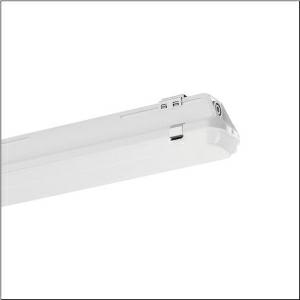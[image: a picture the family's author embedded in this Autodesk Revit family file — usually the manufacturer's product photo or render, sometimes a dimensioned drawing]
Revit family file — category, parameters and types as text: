
# Revit family: monsun_r__12_51fp209p460h_750e
name_source: partatom
category: Lighting Fixtures
units: mm (PartAtom-declared; Revit-internal decimal feet)

## family parameters
Cut with Voids When Loaded = No
Host = Face
Light Source = No
Part Type = Normal
Room Calculation Point = No
Round Connector Dimension = Use Diameter
Shared = No

## types (1)
- Monsun® 12 (1 x LED, 5490 lm, 34 W, 4000K)
    Apparent Load = 34 VA
    CIE Flux Codes = 45 75 93 94 100
    Color Rendering = 80
    Color Temperature = 4000K
    Default Elevation = 1800 mm
    Description = Monsun® 12, damp-proof luminaire, chain hanger, primary optical cover: enclosure, of PC, light emission: direct distribution, primary light characteristic: symmetric, installation type: suspended mounting, surface-mounted, horizontal mounting, vertical mounting, LED rated luminous flux: 5.490 lm, light colour: 840, colour temperature: 4000K, control gear: ECG, with terminal, 3-pole, max. 2.5mm², mains connection: 220..240V, AC, 50/60Hz, rated input power: 34W, luminaire housing, of glass-fibre reinforced polyester, uncoated, bright grey, length: 1.590 mm, width: 90 mm, height: 88mm, clip for enclosure, of stainless steel (V2A), ceiling mounting element, of stainless steel (V2A), chain hanger, of stainless steel (V2A), protection rating (complete): IP66, insulation class (complete): insulation class I (protective earthing), certification: CE, ENEC, VDE, protection symbol: D, impact resistance: IK08, permissible ambient temperature for indoor applications: -35..+40°C, standard: EN 50419, EN 60598-2-1, no direct snow, no direct sun, no direct rain, for indoor or canopied outdoor use, corresponds to IFS (International Featured Standards) requirements for safety and quality in the food industry, packaging unit: 1 piece
    Height = 89 mm
    Lamp = 1 x LED
    Lamp Light Flux = 5490 lm
    Lamp Power = 34 W
    Lamp count = 1
    Length = 1590 mm
    Luminous efficacy = 161 lm/W
    Manufacturer = Siteco
    ModVariant = No
    Model = 51FP209P460H
    Mounting Place = Ceiling
    Mounting Type = Pendant
    Number of Poles = 1
    OnlyDefault = Yes
    Power Factor = 1
    Product Name = Monsun® 12
    Product group = damp-proof luminaire | ceiling pendant
    ProductGroupID = 908
    Protection Class = Protection class I
    Protection Degree = IP 66
    RLX_Detail_Level = 1
    RlxData = <blob elided: 88121 chars, md5=bcb575e1>
    Socket = socket
    Standby Power = 0 W
    System Light Flux = 5490 lm
    System Power = 34 W
    Type Comments = Product without accessories
    Type Image = l_1004748.jpg
    URL = http://relux.com
    VarID = ---
    Voltage = 0 V
    Weight = 0.00 kg
    Width = 90 mm

## geometry (parser evidence)
native form markers: Blend x4, Sweep x14
no freeform markers — native parametric forms only
